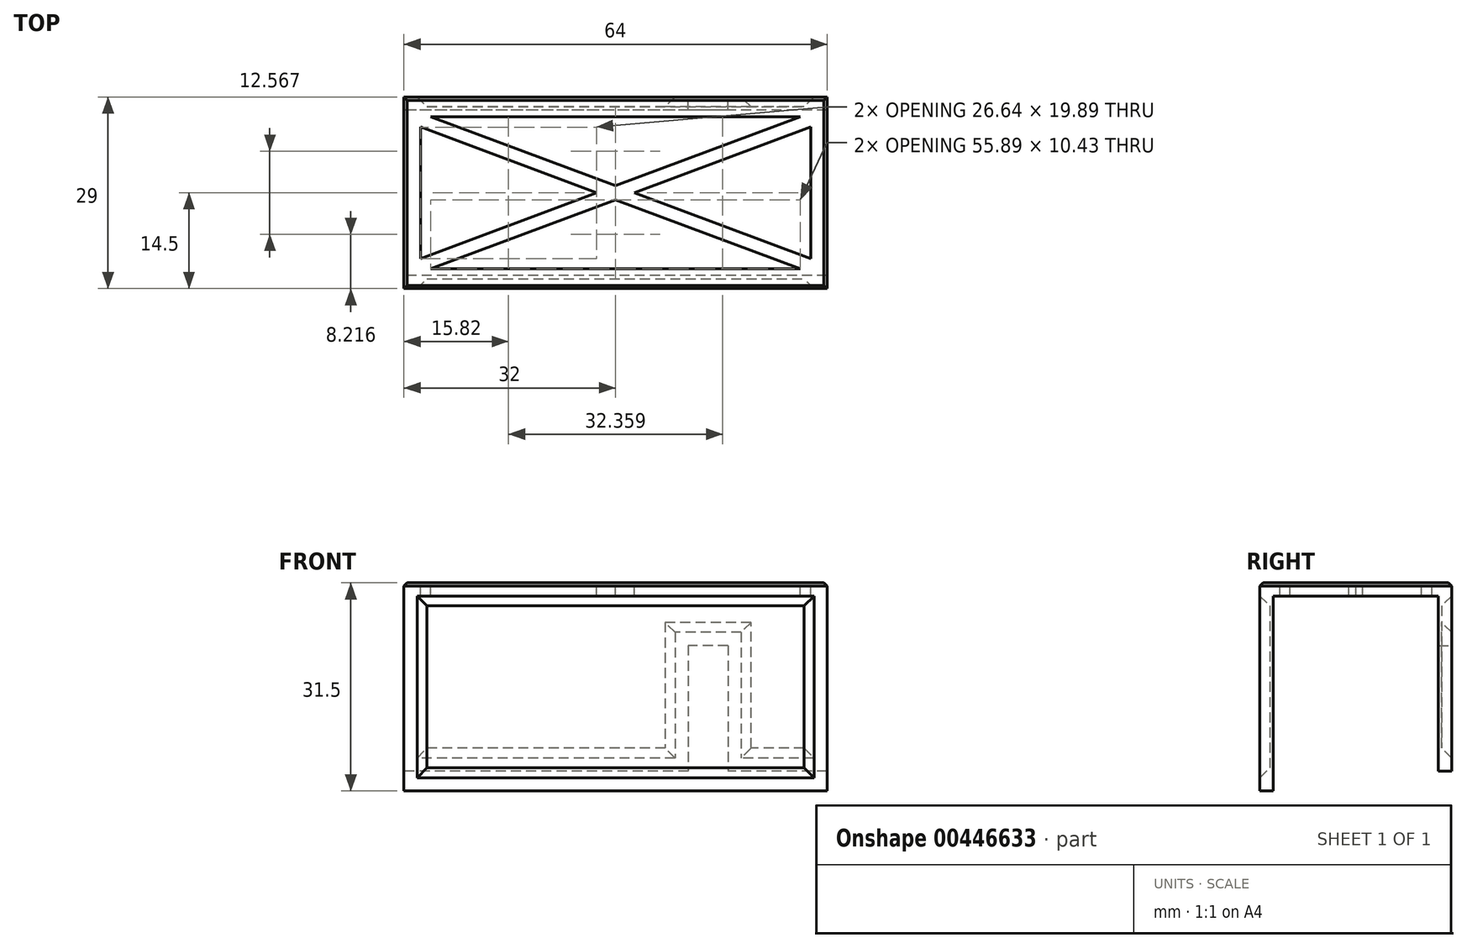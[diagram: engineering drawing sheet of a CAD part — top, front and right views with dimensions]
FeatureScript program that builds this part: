
annotation { "Feature Type Name" : "Feature", "Feature Type Description" : "" }
export const myFeature = defineFeature(function(context is Context, id is Id, definition is map)
    precondition{}
    {
        {
            var Q0;
            Q0=qCreatedBy(makeId("Right.planeOp"),FACE);
            var sketch = newSketch(context, id + "F0", { "sketchPlane" : qUnion([Q0])});
            skLineSegment(sketch, "E0.top", {"start": v(-12.5, 29.5) * mm, "end": v(12.5, 29.5) * mm});
            skLineSegment(sketch, "E0.left", {"start": v(-12.5, 0) * mm, "end": v(-12.5, 29.5) * mm});
            skLineSegment(sketch, "E0.right", {"start": v(12.5, 3) * mm, "end": v(12.5, 29.5) * mm});
            skLineSegment(sketch, "E1.0", {"start": v(-14.5, 0) * mm, "end": v(-14.5, 31.5) * mm});
            skLineSegment(sketch, "E1.1", {"start": v(-14.5, 31.5) * mm, "end": v(14.5, 31.5) * mm});
            skLineSegment(sketch, "E1.2", {"start": v(14.5, 3) * mm, "end": v(14.5, 31.5) * mm});
            skLineSegment(sketch, "E2", {"start": v(-14.5, 0) * mm, "end": v(-12.5, 0) * mm});
            skLineSegment(sketch, "E3", {"start": v(12.5, 3) * mm, "end": v(14.5, 3) * mm});
            skLineSegment(sketch, "E4", {"start": v(0, 0) * mm, "end": v(0, 29.5) * mm, "construction": true});
            skSolve(sketch);
        }
        {
            var Q0;
            Q0=makeQuery(id+"F0.imprint","IMPRINT",FACE,{"disambiguationData":[TD([[makeQuery(id+"F0.imprint","IMPRINT",EDGE,{"derivedFrom":sQuery(id+"F0.wireOp",EDGE,"E0.top")}),1.0]])]});
            extrude(context, id + "F1", {"entities" : qUnion([Q0]), "endBound" : BoundingType.SYMMETRIC, "depth" : 64 * mm});
        }
        {
            var Q0;
            Q0=makeQuery(id+"F1.opExtrude","SWEPT_FACE",FACE,{"disambiguationData":[OSD([sQuery(id+"F0.wireOp",EDGE,"E1.2")])]});
            var sketch = newSketch(context, id + "F2", { "sketchPlane" : qUnion([Q0])});
            skLineSegment(sketch, "E5.bottom", {"start": v(-17, 22) * mm, "end": v(-11, 22) * mm});
            skLineSegment(sketch, "E5.top", {"start": v(-17, 3) * mm, "end": v(-11, 3) * mm});
            skLineSegment(sketch, "E5.left", {"start": v(-17, 22) * mm, "end": v(-17, 3) * mm});
            skLineSegment(sketch, "E5.right", {"start": v(-11, 22) * mm, "end": v(-11, 3) * mm});
            skLineSegment(sketch, "E6.0.0", {"start": v(32, 3) * mm, "end": v(32, 31.5) * mm, "construction": true});
            skLineSegment(sketch, "E6.0.1", {"start": v(32, 31.5) * mm, "end": v(-32, 31.5) * mm, "construction": true});
            skLineSegment(sketch, "E6.0.2", {"start": v(-32, 31.5) * mm, "end": v(-32, 3) * mm, "construction": true});
            skLineSegment(sketch, "E6.0.3", {"start": v(-32, 3) * mm, "end": v(32, 3) * mm, "construction": true});
            skLineSegment(sketch, "E7.0", {"start": v(30, 5) * mm, "end": v(30, 29.5) * mm});
            skLineSegment(sketch, "E7.1", {"start": v(-30, 5) * mm, "end": v(-19, 5) * mm});
            skLineSegment(sketch, "E7.2", {"start": v(-30, 29.5) * mm, "end": v(-30, 5) * mm});
            skLineSegment(sketch, "E7.3", {"start": v(30, 29.5) * mm, "end": v(-30, 29.5) * mm});
            skPoint(sketch, "E8", {"position": v(0, 29.5) * mm});
            skLineSegment(sketch, "E9.0", {"start": v(-9, 24) * mm, "end": v(-9, 5) * mm});
            skLineSegment(sketch, "E9.1", {"start": v(-19, 24) * mm, "end": v(-9, 24) * mm});
            skLineSegment(sketch, "E9.2", {"start": v(-19, 24) * mm, "end": v(-19, 5) * mm});
            skLineSegment(sketch, "E10.trimOffspring", {"start": v(-9, 5) * mm, "end": v(30, 5) * mm});
            skSolve(sketch);
        }
        {
            var Q0;
            Q0=makeQuery(id+"F2.imprint","IMPRINT",FACE,{"disambiguationData":[TD([[makeQuery(id+"F2.imprint","IMPRINT",EDGE,{"derivedFrom":sQuery(id+"F2.wireOp",EDGE,"E7.0")}),1.0]])]});
            extrude(context, id + "F3", {"entities" : qUnion([Q0]), "operationType" : NewBodyOperationType.REMOVE, "oppositeDirection" : true, "depth" : 1.5 * mm});
        }
        {
            var Q0;
            Q0=makeQuery(id+"F2.imprint","IMPRINT",FACE,{"disambiguationData":[TD([[makeQuery(id+"F2.imprint","IMPRINT",EDGE,{"derivedFrom":sQuery(id+"F2.wireOp",EDGE,"E5.bottom")}),-1.0]])]});
            extrude(context, id + "F4", {"entities" : qUnion([Q0]), "operationType" : NewBodyOperationType.REMOVE, "oppositeDirection" : true, "depth" : 2 * mm});
        }
        {
            var Q0;
            Q0=makeQuery(id+"F1.opExtrude","SWEPT_FACE",FACE,{"disambiguationData":[OSD([sQuery(id+"F0.wireOp",EDGE,"E1.0")])]});
            var sketch = newSketch(context, id + "F5", { "sketchPlane" : qUnion([Q0])});
            skLineSegment(sketch, "E11.0", {"start": v(-30, 29.5) * mm, "end": v(-30, 2) * mm});
            skLineSegment(sketch, "E11.1", {"start": v(30, 29.5) * mm, "end": v(-30, 29.5) * mm});
            skLineSegment(sketch, "E11.2", {"start": v(30, 2) * mm, "end": v(30, 29.5) * mm});
            skLineSegment(sketch, "E11.3", {"start": v(-30, 2) * mm, "end": v(30, 2) * mm});
            skSolve(sketch);
        }
        {
            var Q0;
            Q0=makeQuery(id+"F5.imprint","IMPRINT",FACE,{"disambiguationData":[TD([[makeQuery(id+"F5.imprint","IMPRINT",EDGE,{"derivedFrom":sQuery(id+"F5.wireOp",EDGE,"E11.0")}),1.0]])]});
            extrude(context, id + "F6", {"entities" : qUnion([Q0]), "operationType" : NewBodyOperationType.REMOVE, "oppositeDirection" : true, "depth" : 1.5 * mm});
        }
        {
            var Q0;
            Q0=makeQuery(id+"F3.boolean.opBoolean","COPY",EDGE,{"derivedFrom":makeQuery(id+"F3.opExtrude","CAP_EDGE",EDGE,{"disambiguationData":[OSD([sQuery(id+"F2.wireOp",EDGE,"E7.0")])],"isStart":false})});
            var Q1;
            Q1=makeQuery(id+"F3.boolean.opBoolean","COPY",EDGE,{"derivedFrom":makeQuery(id+"F3.opExtrude","CAP_EDGE",EDGE,{"disambiguationData":[OSD([sQuery(id+"F2.wireOp",EDGE,"E7.3")])],"isStart":false})});
            var Q2;
            Q2=makeQuery(id+"F3.boolean.opBoolean","COPY",EDGE,{"derivedFrom":makeQuery(id+"F3.opExtrude","CAP_EDGE",EDGE,{"disambiguationData":[OSD([sQuery(id+"F2.wireOp",EDGE,"E7.2")])],"isStart":false})});
            var Q3;
            Q3=makeQuery(id+"F3.boolean.opBoolean","COPY",EDGE,{"derivedFrom":makeQuery(id+"F3.opExtrude","CAP_EDGE",EDGE,{"disambiguationData":[OSD([sQuery(id+"F2.wireOp",EDGE,"E9.0")])],"isStart":false})});
            var Q4;
            Q4=makeQuery(id+"F3.boolean.opBoolean","COPY",FACE,{"derivedFrom":makeQuery(id+"F3.opExtrude","CAP_FACE",FACE,{"disambiguationData":[OSD([sQuery(id+"F2.wireOp",EDGE,"E7.0"),sQuery(id+"F2.wireOp",EDGE,"E7.1"),sQuery(id+"F2.wireOp",EDGE,"E7.2"),sQuery(id+"F2.wireOp",EDGE,"E7.3"),sQuery(id+"F2.wireOp",EDGE,"E9.0"),sQuery(id+"F2.wireOp",EDGE,"E9.1"),sQuery(id+"F2.wireOp",EDGE,"E9.2"),sQuery(id+"F2.wireOp",EDGE,"E10.trimOffspring")])],"isStart":false})});
            var Q5;
            Q5=makeQuery(id+"F6.boolean.opBoolean","COPY",FACE,{"derivedFrom":makeQuery(id+"F6.opExtrude","CAP_FACE",FACE,{"disambiguationData":[OSD([sQuery(id+"F5.wireOp",EDGE,"E11.0"),sQuery(id+"F5.wireOp",EDGE,"E11.1"),sQuery(id+"F5.wireOp",EDGE,"E11.2"),sQuery(id+"F5.wireOp",EDGE,"E11.3")])],"isStart":false})});
            chamfer(context, id + "F7", {"entities" : qUnion([Q0, Q1, Q2, Q3, Q4, Q5]), "width" : 1.5 * mm, "tangentPropagation" : true});
        }
        {
            var Q0;
            Q0=makeQuery(id+"F1.opExtrude","SWEPT_EDGE",EDGE,{"disambiguationData":[OSD([sQuery(id+"F0.wireOp",EDGE,"E1.1"),sQuery(id+"F0.wireOp",EDGE,"E1.2")])]});
            var Q1;
            Q1=makeQuery(id+"F1.opExtrude","SWEPT_EDGE",EDGE,{"disambiguationData":[OSD([sQuery(id+"F0.wireOp",EDGE,"E1.0"),sQuery(id+"F0.wireOp",EDGE,"E1.1")])]});
            var Q2;
            Q2=makeQuery(id+"F1.opExtrude","CAP_EDGE",EDGE,{"disambiguationData":[OSD([sQuery(id+"F0.wireOp",EDGE,"E1.1")])],"isStart":false});
            var Q3;
            Q3=makeQuery(id+"F1.opExtrude","CAP_EDGE",EDGE,{"disambiguationData":[OSD([sQuery(id+"F0.wireOp",EDGE,"E1.1")])],"isStart":true});
            chamfer(context, id + "F8", {"entities" : qUnion([Q0, Q1, Q2, Q3]), "width" : .5 * mm, "tangentPropagation" : true});
        }
        {
            var Q0;
            Q0=makeQuery(id+"F1.opExtrude","SWEPT_FACE",FACE,{"disambiguationData":[OSD([sQuery(id+"F0.wireOp",EDGE,"E1.1")])]});
            var sketch = newSketch(context, id + "F9", { "sketchPlane" : qUnion([Q0])});
            skLineSegment(sketch, "E12.bottom", {"start": v(-29.5, 11.5) * mm, "end": v(29.5, 11.5) * mm});
            skLineSegment(sketch, "E12.top", {"start": v(-29.5, -11.5) * mm, "end": v(29.5, -11.5) * mm});
            skLineSegment(sketch, "E12.left", {"start": v(-29.5, 11.5) * mm, "end": v(-29.5, -11.5) * mm});
            skLineSegment(sketch, "E12.right", {"start": v(29.5, 11.5) * mm, "end": v(29.5, -11.5) * mm});
            skLineSegment(sketch, "E13.0.0", {"start": v(-31.5, 14) * mm, "end": v(-31.5, -14) * mm});
            skLineSegment(sketch, "E13.0.1", {"start": v(-31.5, -14) * mm, "end": v(31.5, -14) * mm});
            skLineSegment(sketch, "E13.0.2", {"start": v(31.5, -14) * mm, "end": v(31.5, 14) * mm});
            skLineSegment(sketch, "E13.0.3", {"start": v(31.5, 14) * mm, "end": v(-31.5, 14) * mm});
            skLineSegment(sketch, "E14", {"start": v(-29.5, 9.95) * mm, "end": v(-2.86, 0) * mm});
            skLineSegment(sketch, "E15", {"start": v(-2.86, 0) * mm, "end": v(-29.5, -9.95) * mm});
            skLineSegment(sketch, "E16", {"start": v(-27.95, -11.5) * mm, "end": v(0, -1.07) * mm});
            skLineSegment(sketch, "E17", {"start": v(0, -1.07) * mm, "end": v(27.95, -11.5) * mm});
            skLineSegment(sketch, "E18", {"start": v(-27.95, 11.5) * mm, "end": v(0, 1.07) * mm});
            skLineSegment(sketch, "E19", {"start": v(0, 1.07) * mm, "end": v(27.95, 11.5) * mm});
            skLineSegment(sketch, "E20", {"start": v(29.5, 9.95) * mm, "end": v(2.86, 0) * mm});
            skLineSegment(sketch, "E21", {"start": v(2.86, 0) * mm, "end": v(29.5, -9.95) * mm});
            skLineSegment(sketch, "E22", {"start": v(27.95, 11.5) * mm, "end": v(29.5, 9.95) * mm, "construction": true});
            skSolve(sketch);
        }
        {
            var Q0;
            {var subQ0=sQuery(id+"F9.wireOp",EDGE,"E18");Q0=makeQuery(id+"F9.imprint","IMPRINT",FACE,{"disambiguationData":[TD([[makeQuery(id+"F9.imprint","IMPRINT",EDGE,{"derivedFrom":subQ0}),1.0]])]});}
            var Q1;
            {var subQ0=sQuery(id+"F9.wireOp",EDGE,"E14");Q1=makeQuery(id+"F9.imprint","IMPRINT",FACE,{"disambiguationData":[TD([[makeQuery(id+"F9.imprint","IMPRINT",EDGE,{"derivedFrom":subQ0}),-1.0]])]});}
            var Q2;
            {var subQ0=sQuery(id+"F9.wireOp",EDGE,"E16");Q2=makeQuery(id+"F9.imprint","IMPRINT",FACE,{"disambiguationData":[TD([[makeQuery(id+"F9.imprint","IMPRINT",EDGE,{"derivedFrom":subQ0}),-1.0]])]});}
            var Q3;
            {var subQ0=sQuery(id+"F9.wireOp",EDGE,"E20");Q3=makeQuery(id+"F9.imprint","IMPRINT",FACE,{"disambiguationData":[TD([[makeQuery(id+"F9.imprint","IMPRINT",EDGE,{"derivedFrom":subQ0}),1.0]])]});}
            extrude(context, id + "F10", {"entities" : qUnion([Q0, Q1, Q2, Q3]), "operationType" : NewBodyOperationType.REMOVE, "oppositeDirection" : true, "depth" : 2 * mm});
        }
    });
